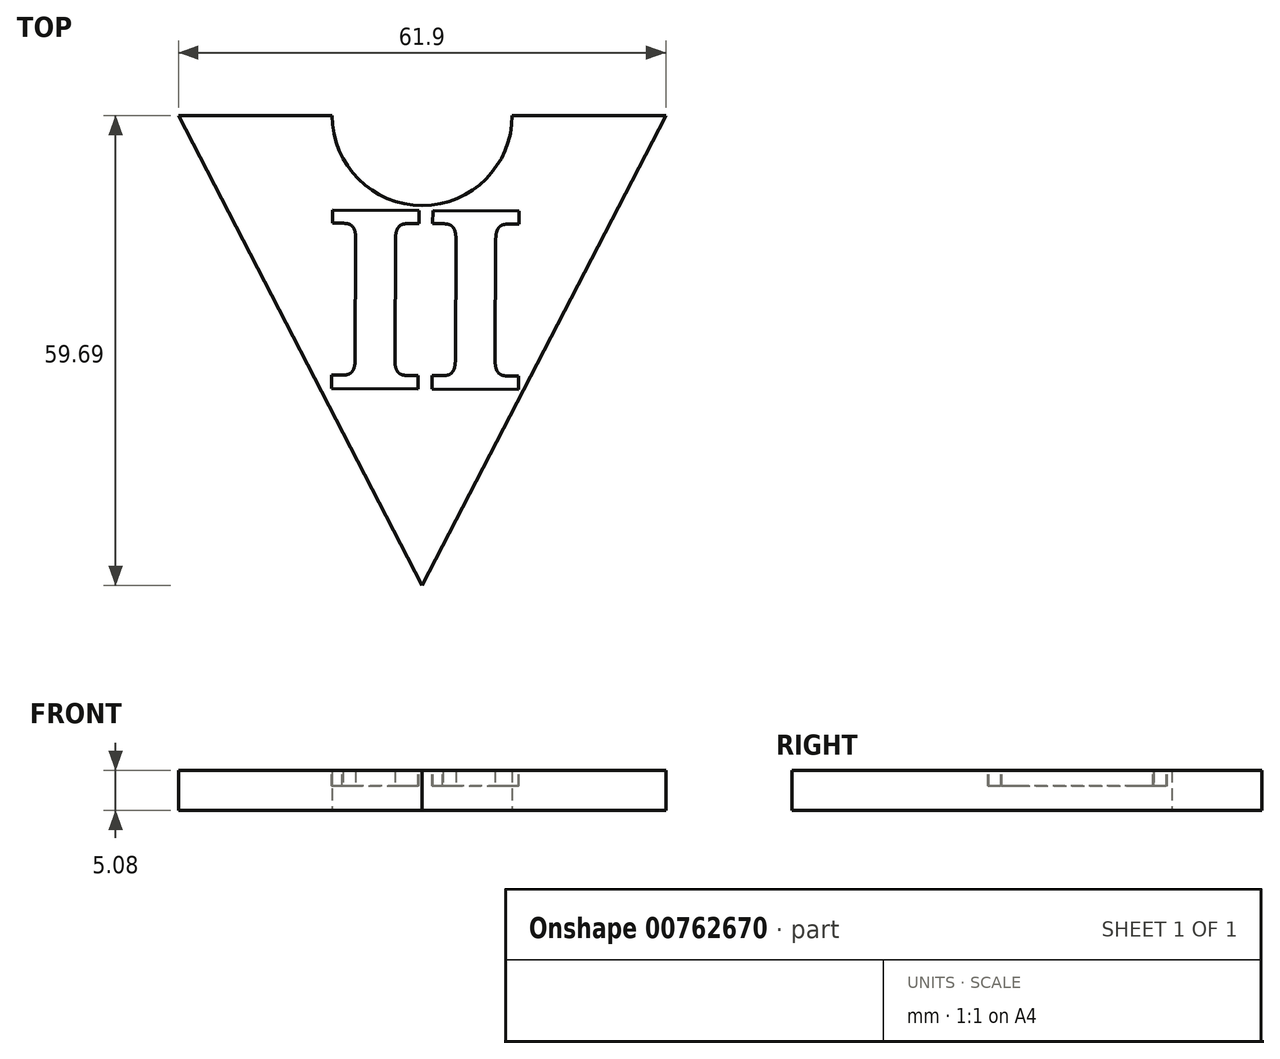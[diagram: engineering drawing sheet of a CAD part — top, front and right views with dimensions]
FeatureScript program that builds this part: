
annotation { "Feature Type Name" : "Feature", "Feature Type Description" : "" }
export const myFeature = defineFeature(function(context is Context, id is Id, definition is map)
    precondition{}
    {
        {
            var Q0;
            Q0=qCreatedBy(makeId("Top.planeOp"),FACE);
            var sketch = newSketch(context, id + "F0", { "sketchPlane" : qUnion([Q0])});
            skCircle(sketch, "E0.cCircle", {"center": v(0, -7.56) * mm, "radius": 17.87 * mm, "construction": true});
            skLineSegment(sketch, "E0.0", {"start": v(-30.95, 10.31) * mm, "end": v(30.95, 10.31) * mm});
            skLineSegment(sketch, "E0.1", {"start": v(30.95, 10.31) * mm, "end": v(0, -49.38) * mm});
            skLineSegment(sketch, "E0.2", {"start": v(0, -49.38) * mm, "end": v(-30.95, 10.31) * mm});
            skPoint(sketch, "E0.0.midPoint", {"position": v(0, 10.31) * mm});
            skSolve(sketch);
        }
        {
            var Q0;
            Q0 = qSketchRegion(id + "F0", true);
            extrude(context, id + "F1", {"entities" : qUnion([Q0]), "depth" : 5.08 * mm, "offsetDistance" : 25.4 * mm});
        }
        {
            var Q0;
            Q0=sQuery(id+"F0.wireOp",VERTEX,"E0.0.midPoint");
            var Q1;
            Q1=makeQuery(id+"F1.opExtrude","SWEPT_BODY",BODY,{"disambiguationData":[OSD([sQuery(id+"F0.wireOp",EDGE,"E0.0"),sQuery(id+"F0.wireOp",EDGE,"E0.1"),sQuery(id+"F0.wireOp",EDGE,"E0.2")])]});
            hole(context, id + "F2", {"style" : HoleStyle.SIMPLE, "endStyle" : HoleEndStyle.THROUGH, "oppositeDirection" : true, "holeDiameter" : 22.86 * mm, "majorDiameter" : 6.35 * mm, "isTappedThrough" : true, "tappedDepth" : 12.7 * mm, "tapClearance" : 3, "locations" : qUnion([Q0]), "scope" : qUnion([Q1])});
        }
        {
            var Q0;
            Q0=makeQuery(id+"F1.opExtrude","CAP_FACE",FACE,{"disambiguationData":[OSD([sQuery(id+"F0.wireOp",EDGE,"E0.0"),sQuery(id+"F0.wireOp",EDGE,"E0.1"),sQuery(id+"F0.wireOp",EDGE,"E0.2")])],"isStart":false});
            var sketch = newSketch(context, id + "F3", { "sketchPlane" : qUnion([Q0])});
            skText(sketch, "E1", { "text": "II", "fontName": "NotoSerif-Bold.ttf"});
            skPoint(sketch, "E1.secondSnap0", {"position": v(-21.19, 10.31) * mm});
            const initialGuessF3  = {"E1": [-0.01238, -0.02435, 0.99999, -0.00509, 0.02287]};
            skSetInitialGuess(sketch, initialGuessF3);
            skSolve(sketch);
        }
        {
            var Q0;
            Q0 = qSketchRegion(id + "F3", true);
            extrude(context, id + "F4", {"entities" : qUnion([Q0]), "operationType" : NewBodyOperationType.REMOVE, "oppositeDirection" : true, "depth" : 2 * mm, "offsetDistance" : 25.4 * mm});
        }
    });
